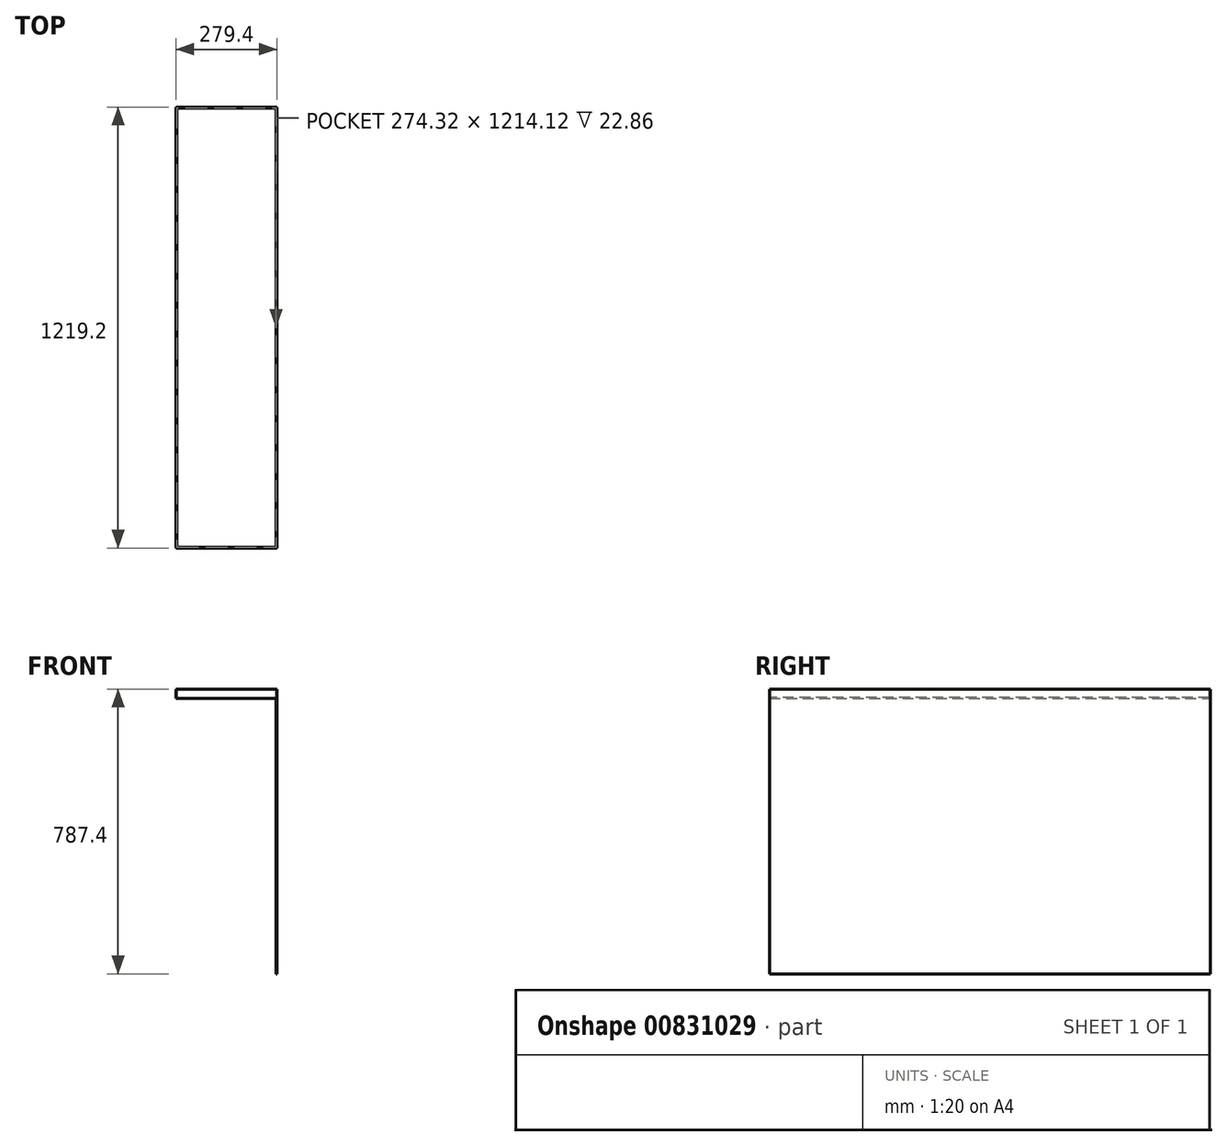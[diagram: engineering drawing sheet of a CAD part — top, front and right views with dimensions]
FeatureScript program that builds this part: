
annotation { "Feature Type Name" : "Feature", "Feature Type Description" : "" }
export const myFeature = defineFeature(function(context is Context, id is Id, definition is map)
    precondition{}
    {
        {
            var Q0;
            Q0=qCreatedBy(makeId("Front.planeOp"),FACE);
            var sketch = newSketch(context, id + "F0", { "sketchPlane" : qUnion([Q0])});
            skLineSegment(sketch, "E0", {"start": v(0, 0) * mm, "end": v(0, 787.4) * mm});
            skLineSegment(sketch, "E1", {"start": v(0, 787.4) * mm, "end": v(-279.4, 787.4) * mm});
            skLineSegment(sketch, "E2", {"start": v(-279.4, 787.4) * mm, "end": v(-279.4, 762) * mm});
            skLineSegment(sketch, "E3", {"start": v(-279.4, 762) * mm, "end": v(-2.54, 762) * mm});
            skLineSegment(sketch, "E4", {"start": v(-2.54, 762) * mm, "end": v(-2.54, 0) * mm});
            skLineSegment(sketch, "E5", {"start": v(-2.54, 0) * mm, "end": v(0, 0) * mm});
            skSolve(sketch);
        }
        {
            var Q0;
            Q0=makeQuery(id+"F0.imprint","IMPRINT",FACE,{"disambiguationData":[TD([[makeQuery(id+"F0.imprint","IMPRINT",EDGE,{"derivedFrom":sQuery(id+"F0.wireOp",EDGE,"E0")}),1.0]])]});
            extrude(context, id + "F1", {"entities" : qUnion([Q0]), "depth" : 1219.2 * mm, "offsetDistance" : 25.4 * mm});
        }
        {
            var Q0;
            Q0=makeQuery(id+"F1.opExtrude","SWEPT_FACE",FACE,{"disambiguationData":[OSD([sQuery(id+"F0.wireOp",EDGE,"E1")])]});
            shell(context, id + "F2", {"entities" : qUnion([Q0]), "thickness" : 2.54 * mm});
        }
    });
